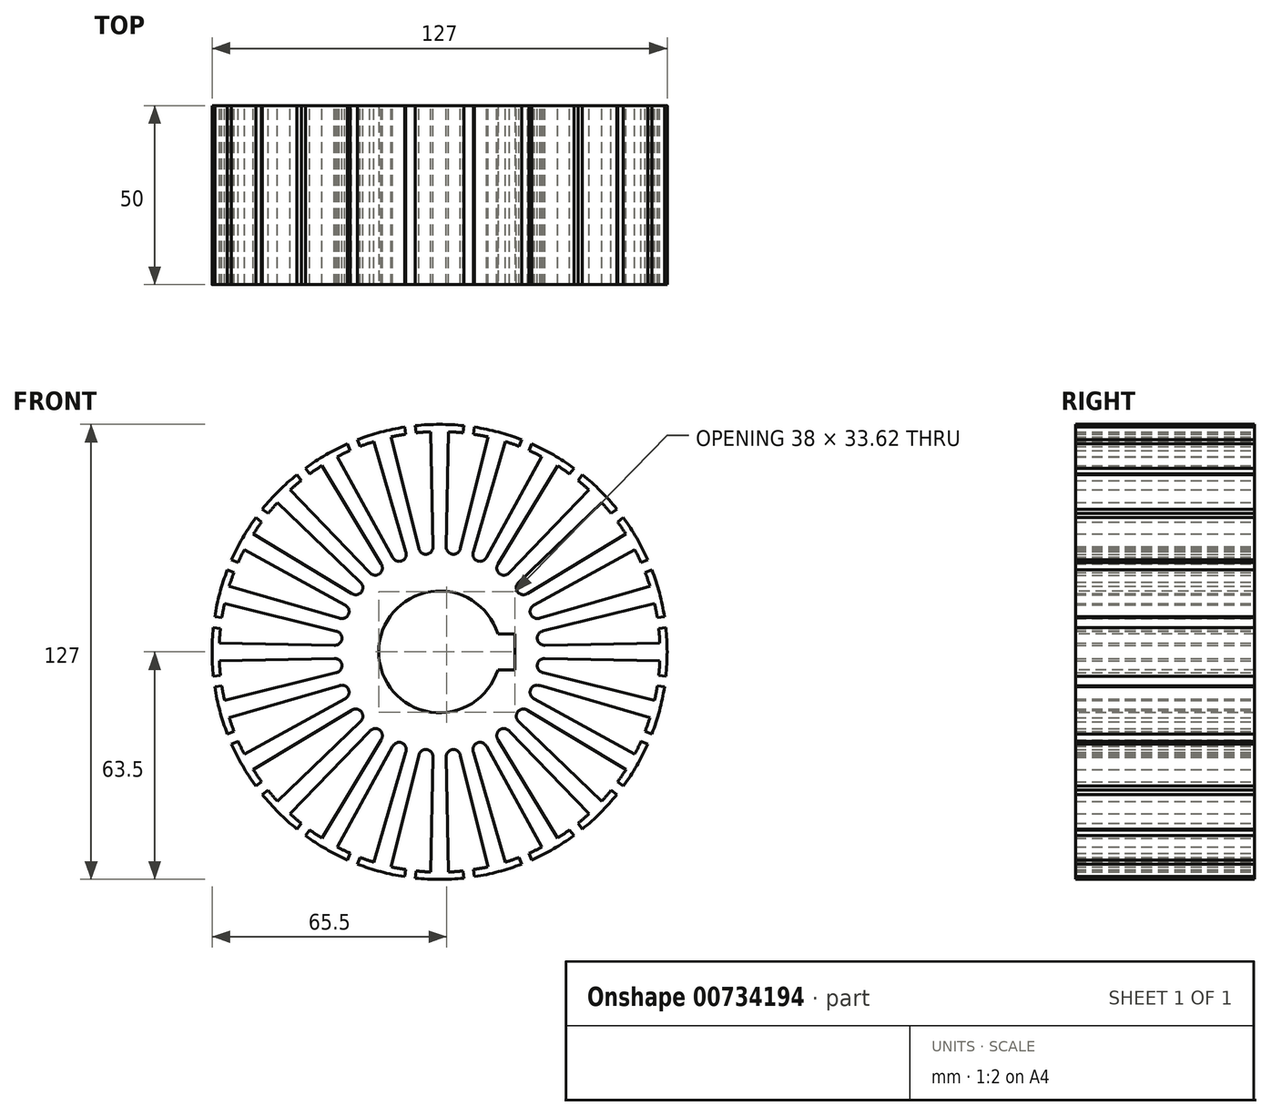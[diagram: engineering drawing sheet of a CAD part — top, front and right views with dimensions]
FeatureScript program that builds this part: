
annotation { "Feature Type Name" : "Feature", "Feature Type Description" : "" }
export const myFeature = defineFeature(function(context is Context, id is Id, definition is map)
    precondition{}
    {
        {
            var Q0;
            Q0=qCreatedBy(makeId("Front.planeOp"),FACE);
            var sketch = newSketch(context, id + "F0", { "sketchPlane" : qUnion([Q0])});
            skCircle(sketch, "E0", {"center": v(0, 0) * mm, "radius": 17 * mm});
            skArc(sketch, "E1", {"start": v(-9.51, 60.76) * mm, "mid": v(-11.5, 60.41) * mm, "end": v(-13.48, 60) * mm});
            skArc(sketch, "E2", {"start": v(1.86, 29.44) * mm, "mid": v(2.28, 28) * mm, "end": v(3.59, 27.26) * mm});
            skArc(sketch, "E3.MirrorC", {"start": v(-1.86, 29.44) * mm, "mid": v(-2.28, 28) * mm, "end": v(-3.59, 27.26) * mm});
            skArc(sketch, "E4.MirrorC", {"start": v(13.1, 26.43) * mm, "mid": v(10.52, 25.4) * mm, "end": v(9.42, 27.96) * mm});
            skArc(sketch, "E5.MirrorC", {"start": v(16.33, 24.57) * mm, "mid": v(16.74, 21.82) * mm, "end": v(19.5, 22.13) * mm});
            skArc(sketch, "E6.MirrorC", {"start": v(24.57, 16.33) * mm, "mid": v(23.1, 15.98) * mm, "end": v(21.82, 16.74) * mm});
            skArc(sketch, "E7.MirrorC", {"start": v(26.43, 13.1) * mm, "mid": v(25.4, 10.52) * mm, "end": v(27.96, 9.42) * mm});
            skArc(sketch, "E8.MirrorC", {"start": v(29.44, 1.86) * mm, "mid": v(27.26, 3.59) * mm, "end": v(28.92, 5.82) * mm});
            skArc(sketch, "E9.MirrorC", {"start": v(29.44, -1.86) * mm, "mid": v(27.26, -3.59) * mm, "end": v(28.92, -5.82) * mm});
            skArc(sketch, "E10.MirrorC", {"start": v(26.43, -13.1) * mm, "mid": v(25.4, -10.52) * mm, "end": v(27.96, -9.42) * mm});
            skArc(sketch, "E11.MirrorC", {"start": v(24.57, -16.33) * mm, "mid": v(21.82, -16.74) * mm, "end": v(22.13, -19.5) * mm});
            skArc(sketch, "E12.MirrorC", {"start": v(16.33, -24.57) * mm, "mid": v(16.74, -21.82) * mm, "end": v(19.5, -22.13) * mm});
            skArc(sketch, "E13.MirrorC", {"start": v(13.1, -26.43) * mm, "mid": v(10.52, -25.4) * mm, "end": v(9.42, -27.96) * mm});
            skArc(sketch, "E14.MirrorC", {"start": v(1.86, -29.44) * mm, "mid": v(3.59, -27.26) * mm, "end": v(5.82, -28.92) * mm});
            skArc(sketch, "E15.MirrorC", {"start": v(-1.86, -29.44) * mm, "mid": v(-3.59, -27.26) * mm, "end": v(-5.82, -28.92) * mm});
            skArc(sketch, "E16.MirrorC", {"start": v(-13.1, -26.43) * mm, "mid": v(-10.52, -25.4) * mm, "end": v(-9.42, -27.96) * mm});
            skArc(sketch, "E17.MirrorC", {"start": v(-16.33, -24.57) * mm, "mid": v(-16.74, -21.82) * mm, "end": v(-19.5, -22.13) * mm});
            skArc(sketch, "E18.MirrorC", {"start": v(-24.57, -16.33) * mm, "mid": v(-21.82, -16.74) * mm, "end": v(-22.13, -19.5) * mm});
            skArc(sketch, "E19.MirrorC", {"start": v(-26.43, -13.1) * mm, "mid": v(-25.4, -10.52) * mm, "end": v(-27.96, -9.42) * mm});
            skArc(sketch, "E20.MirrorC", {"start": v(-29.44, -1.86) * mm, "mid": v(-27.26, -3.59) * mm, "end": v(-28.92, -5.82) * mm});
            skArc(sketch, "E21.MirrorC", {"start": v(-29.44, 1.86) * mm, "mid": v(-27.26, 3.59) * mm, "end": v(-28.92, 5.82) * mm});
            skArc(sketch, "E22.MirrorC", {"start": v(-26.43, 13.1) * mm, "mid": v(-25.4, 10.52) * mm, "end": v(-27.96, 9.42) * mm});
            skArc(sketch, "E23.MirrorC", {"start": v(-24.57, 16.33) * mm, "mid": v(-21.82, 16.74) * mm, "end": v(-22.13, 19.5) * mm});
            skArc(sketch, "E24.MirrorC", {"start": v(-13.1, 26.43) * mm, "mid": v(-10.52, 25.4) * mm, "end": v(-9.42, 27.96) * mm});
            skArc(sketch, "E25.MirrorC", {"start": v(-16.33, 24.57) * mm, "mid": v(-16.74, 21.82) * mm, "end": v(-19.5, 22.13) * mm});
            skLineSegment(sketch, "E26", {"start": v(-2.5, 61.45) * mm, "end": v(-1.86, 29.44) * mm});
            skLineSegment(sketch, "E27", {"start": v(2.5, 61.45) * mm, "end": v(1.85, 29.44) * mm});
            skLineSegment(sketch, "E28.MirrorCS", {"start": v(13.49, 60) * mm, "end": v(5.83, 28.92) * mm});
            skLineSegment(sketch, "E29.MirrorCS", {"start": v(-13.48, 60) * mm, "end": v(-5.82, 28.92) * mm});
            skLineSegment(sketch, "E30.MirrorCS", {"start": v(18.32, 58.7) * mm, "end": v(9.41, 27.96) * mm});
            skLineSegment(sketch, "E31.MirrorCS", {"start": v(28.56, 54.47) * mm, "end": v(13.12, 26.42) * mm});
            skLineSegment(sketch, "E32.MirrorCS", {"start": v(32.9, 51.96) * mm, "end": v(16.33, 24.57) * mm});
            skLineSegment(sketch, "E33.MirrorCS", {"start": v(41.68, 45.22) * mm, "end": v(19.5, 22.13) * mm});
            skLineSegment(sketch, "E34.MirrorCS", {"start": v(45.22, 41.68) * mm, "end": v(22.13, 19.5) * mm});
            skLineSegment(sketch, "E35.MirrorCS", {"start": v(54.47, 28.56) * mm, "end": v(26.42, 13.12) * mm});
            skLineSegment(sketch, "E36.MirrorCS", {"start": v(58.7, 18.32) * mm, "end": v(27.96, 9.41) * mm});
            skLineSegment(sketch, "E37.MirrorCS", {"start": v(60, 13.49) * mm, "end": v(28.92, 5.83) * mm});
            skLineSegment(sketch, "E38.MirrorCS", {"start": v(61.45, 2.5) * mm, "end": v(29.44, 1.85) * mm});
            skLineSegment(sketch, "E39.MirrorCS", {"start": v(61.45, -2.5) * mm, "end": v(29.44, -1.86) * mm});
            skLineSegment(sketch, "E40.MirrorCS", {"start": v(60, -13.48) * mm, "end": v(28.92, -5.82) * mm});
            skLineSegment(sketch, "E41.MirrorCS", {"start": v(58.7, -18.33) * mm, "end": v(27.96, -9.42) * mm});
            skLineSegment(sketch, "E42.MirrorCS", {"start": v(54.47, -28.55) * mm, "end": v(26.43, -13.1) * mm});
            skLineSegment(sketch, "E43.MirrorCS", {"start": v(51.97, -32.89) * mm, "end": v(24.57, -16.33) * mm});
            skLineSegment(sketch, "E44.MirrorCS", {"start": v(45.22, -41.68) * mm, "end": v(22.13, -19.5) * mm});
            skLineSegment(sketch, "E45.MirrorCS", {"start": v(41.68, -45.22) * mm, "end": v(19.5, -22.13) * mm});
            skLineSegment(sketch, "E46.MirrorCS", {"start": v(32.89, -51.97) * mm, "end": v(16.33, -24.57) * mm});
            skLineSegment(sketch, "E47.MirrorCS", {"start": v(51.96, 32.9) * mm, "end": v(24.57, 16.33) * mm});
            skLineSegment(sketch, "E48.MirrorCS", {"start": v(28.56, -54.47) * mm, "end": v(13.12, -26.42) * mm});
            skLineSegment(sketch, "E49.MirrorCS", {"start": v(18.32, -58.7) * mm, "end": v(9.41, -27.96) * mm});
            skLineSegment(sketch, "E50.MirrorCS", {"start": v(13.49, -60) * mm, "end": v(5.83, -28.92) * mm});
            skLineSegment(sketch, "E51.MirrorCS", {"start": v(2.5, -61.45) * mm, "end": v(1.85, -29.44) * mm});
            skLineSegment(sketch, "E52.MirrorCS", {"start": v(-2.5, -61.45) * mm, "end": v(-1.85, -29.44) * mm});
            skLineSegment(sketch, "E53.MirrorCS", {"start": v(-13.49, -60) * mm, "end": v(-5.83, -28.92) * mm});
            skLineSegment(sketch, "E54.MirrorCS", {"start": v(-18.32, -58.7) * mm, "end": v(-9.41, -27.96) * mm});
            skLineSegment(sketch, "E55.MirrorCS", {"start": v(-28.56, -54.47) * mm, "end": v(-13.12, -26.42) * mm});
            skLineSegment(sketch, "E56.MirrorCS", {"start": v(-32.89, -51.97) * mm, "end": v(-16.33, -24.57) * mm});
            skLineSegment(sketch, "E57.MirrorCS", {"start": v(-41.68, -45.22) * mm, "end": v(-19.5, -22.13) * mm});
            skLineSegment(sketch, "E58.MirrorCS", {"start": v(-45.22, -41.68) * mm, "end": v(-22.13, -19.5) * mm});
            skLineSegment(sketch, "E59.MirrorCS", {"start": v(-51.97, -32.89) * mm, "end": v(-24.57, -16.33) * mm});
            skLineSegment(sketch, "E60.MirrorCS", {"start": v(-54.47, -28.56) * mm, "end": v(-26.42, -13.12) * mm});
            skLineSegment(sketch, "E61.MirrorCS", {"start": v(-58.7, -18.32) * mm, "end": v(-27.96, -9.41) * mm});
            skLineSegment(sketch, "E62.MirrorCS", {"start": v(-60, -13.49) * mm, "end": v(-28.92, -5.83) * mm});
            skLineSegment(sketch, "E63.MirrorCS", {"start": v(-61.45, -2.5) * mm, "end": v(-29.44, -1.85) * mm});
            skLineSegment(sketch, "E64.MirrorCS", {"start": v(-61.45, 2.5) * mm, "end": v(-29.44, 1.85) * mm});
            skLineSegment(sketch, "E65.MirrorCS", {"start": v(-60, 13.49) * mm, "end": v(-28.92, 5.83) * mm});
            skLineSegment(sketch, "E66.MirrorCS", {"start": v(-58.7, 18.32) * mm, "end": v(-27.96, 9.41) * mm});
            skLineSegment(sketch, "E67.MirrorCS", {"start": v(-54.47, 28.56) * mm, "end": v(-26.42, 13.12) * mm});
            skLineSegment(sketch, "E68.MirrorCS", {"start": v(-51.97, 32.89) * mm, "end": v(-24.57, 16.33) * mm});
            skLineSegment(sketch, "E69.MirrorCS", {"start": v(-45.22, 41.68) * mm, "end": v(-22.13, 19.5) * mm});
            skLineSegment(sketch, "E70.MirrorCS", {"start": v(-41.68, 45.22) * mm, "end": v(-19.5, 22.13) * mm});
            skLineSegment(sketch, "E71.MirrorCS", {"start": v(-32.89, 51.97) * mm, "end": v(-16.33, 24.57) * mm});
            skLineSegment(sketch, "E72.MirrorCS", {"start": v(-28.56, 54.47) * mm, "end": v(-13.12, 26.42) * mm});
            skLineSegment(sketch, "E73.MirrorCS", {"start": v(-18.32, 58.7) * mm, "end": v(-9.41, 27.96) * mm});
            skArc(sketch, "E74.MirrorCS", {"start": v(22.13, 19.5) * mm, "mid": v(21.42, 18.19) * mm, "end": v(21.82, 16.74) * mm});
            skLineSegment(sketch, "E75.MirrorCS", {"start": v(-6.8, 63.13) * mm, "end": v(-6.54, 61.15) * mm});
            skLineSegment(sketch, "E76.MirrorCS", {"start": v(-9.77, 62.74) * mm, "end": v(-9.51, 60.76) * mm});
            skLineSegment(sketch, "E77.MirrorCS", {"start": v(-22.9, 59.22) * mm, "end": v(-22.14, 57.38) * mm});
            skLineSegment(sketch, "E78.MirrorCS", {"start": v(-25.69, 58.1) * mm, "end": v(-24.91, 56.23) * mm});
            skLineSegment(sketch, "E79.MirrorCS", {"start": v(-37.47, 51.3) * mm, "end": v(-36.24, 49.69) * mm});
            skLineSegment(sketch, "E80.MirrorCS", {"start": v(-39.84, 49.45) * mm, "end": v(-38.62, 47.86) * mm});
            skLineSegment(sketch, "E81.MirrorCS", {"start": v(-49.45, 39.84) * mm, "end": v(-47.86, 38.62) * mm});
            skLineSegment(sketch, "E82.MirrorCS", {"start": v(-51.3, 37.47) * mm, "end": v(-49.69, 36.24) * mm});
            skLineSegment(sketch, "E83.MirrorCS", {"start": v(-59.22, 22.9) * mm, "end": v(-57.38, 22.14) * mm});
            skLineSegment(sketch, "E84.MirrorCS", {"start": v(-58.1, 25.69) * mm, "end": v(-56.23, 24.91) * mm});
            skLineSegment(sketch, "E85.MirrorCS", {"start": v(-62.74, 9.77) * mm, "end": v(-60.76, 9.51) * mm});
            skLineSegment(sketch, "E86.MirrorCS", {"start": v(-63.15, 6.8) * mm, "end": v(-61.15, 6.54) * mm});
            skLineSegment(sketch, "E87.MirrorCS", {"start": v(-63.15, -6.8) * mm, "end": v(-61.15, -6.54) * mm});
            skLineSegment(sketch, "E88.MirrorCS", {"start": v(-62.74, -9.77) * mm, "end": v(-60.76, -9.51) * mm});
            skLineSegment(sketch, "E89.MirrorCS", {"start": v(-59.22, -22.9) * mm, "end": v(-57.38, -22.14) * mm});
            skLineSegment(sketch, "E90.MirrorCS", {"start": v(-58.1, -25.69) * mm, "end": v(-56.23, -24.91) * mm});
            skLineSegment(sketch, "E91.MirrorCS", {"start": v(-51.3, -37.47) * mm, "end": v(-49.69, -36.24) * mm});
            skLineSegment(sketch, "E92.MirrorCS", {"start": v(-49.45, -39.84) * mm, "end": v(-47.86, -38.62) * mm});
            skLineSegment(sketch, "E93.MirrorCS", {"start": v(-39.84, -49.45) * mm, "end": v(-38.62, -47.86) * mm});
            skLineSegment(sketch, "E94.MirrorCS", {"start": v(-37.47, -51.3) * mm, "end": v(-36.24, -49.69) * mm});
            skLineSegment(sketch, "E95.MirrorCS", {"start": v(-25.69, -58.1) * mm, "end": v(-24.91, -56.23) * mm});
            skLineSegment(sketch, "E96.MirrorCS", {"start": v(-22.9, -59.22) * mm, "end": v(-22.14, -57.38) * mm});
            skLineSegment(sketch, "E97.MirrorCS", {"start": v(-9.77, -62.74) * mm, "end": v(-9.51, -60.76) * mm});
            skLineSegment(sketch, "E98.MirrorCS", {"start": v(-6.8, -63.15) * mm, "end": v(-6.54, -61.15) * mm});
            skLineSegment(sketch, "E99.MirrorCS", {"start": v(6.8, -63.15) * mm, "end": v(6.54, -61.15) * mm});
            skLineSegment(sketch, "E100.MirrorCS", {"start": v(9.77, -62.74) * mm, "end": v(9.51, -60.76) * mm});
            skLineSegment(sketch, "E101.MirrorCS", {"start": v(22.9, -59.22) * mm, "end": v(22.14, -57.38) * mm});
            skLineSegment(sketch, "E102.MirrorCS", {"start": v(25.69, -58.1) * mm, "end": v(24.91, -56.23) * mm});
            skLineSegment(sketch, "E103.MirrorCS", {"start": v(37.47, -51.3) * mm, "end": v(36.24, -49.69) * mm});
            skLineSegment(sketch, "E104.MirrorCS", {"start": v(39.84, -49.45) * mm, "end": v(38.62, -47.86) * mm});
            skLineSegment(sketch, "E105.MirrorCS", {"start": v(49.45, -39.84) * mm, "end": v(47.86, -38.62) * mm});
            skLineSegment(sketch, "E106.MirrorCS", {"start": v(51.3, -37.47) * mm, "end": v(49.69, -36.24) * mm});
            skLineSegment(sketch, "E107.MirrorCS", {"start": v(58.1, -25.69) * mm, "end": v(56.23, -24.91) * mm});
            skLineSegment(sketch, "E108.MirrorCS", {"start": v(59.22, -22.9) * mm, "end": v(57.38, -22.14) * mm});
            skLineSegment(sketch, "E109.MirrorCS", {"start": v(63.15, -6.8) * mm, "end": v(61.15, -6.54) * mm});
            skLineSegment(sketch, "E110.MirrorCS", {"start": v(62.74, -9.77) * mm, "end": v(60.76, -9.51) * mm});
            skLineSegment(sketch, "E111.MirrorCS", {"start": v(63.15, 6.8) * mm, "end": v(61.15, 6.54) * mm});
            skLineSegment(sketch, "E112.MirrorCS", {"start": v(62.74, 9.77) * mm, "end": v(60.76, 9.51) * mm});
            skLineSegment(sketch, "E113.MirrorCS", {"start": v(59.22, 22.9) * mm, "end": v(57.38, 22.14) * mm});
            skLineSegment(sketch, "E114.MirrorCS", {"start": v(58.1, 25.69) * mm, "end": v(56.23, 24.91) * mm});
            skLineSegment(sketch, "E115.MirrorCS", {"start": v(51.3, 37.47) * mm, "end": v(49.69, 36.24) * mm});
            skLineSegment(sketch, "E116.MirrorCS", {"start": v(49.45, 39.84) * mm, "end": v(47.86, 38.62) * mm});
            skLineSegment(sketch, "E117.MirrorCS", {"start": v(39.84, 49.45) * mm, "end": v(38.62, 47.86) * mm});
            skLineSegment(sketch, "E118.MirrorCS", {"start": v(37.47, 51.3) * mm, "end": v(36.24, 49.69) * mm});
            skLineSegment(sketch, "E119.MirrorCS", {"start": v(6.8, 63.13) * mm, "end": v(6.54, 61.15) * mm});
            skLineSegment(sketch, "E120.MirrorCS", {"start": v(9.77, 62.74) * mm, "end": v(9.51, 60.76) * mm});
            skLineSegment(sketch, "E121.MirrorCS", {"start": v(22.9, 59.22) * mm, "end": v(22.14, 57.38) * mm});
            skLineSegment(sketch, "E122.MirrorCS", {"start": v(25.69, 58.1) * mm, "end": v(24.91, 56.23) * mm});
            skArc(sketch, "E123.trimOffspring", {"start": v(-24.91, 56.23) * mm, "mid": v(-26.75, 55.38) * mm, "end": v(-28.56, 54.47) * mm});
            skArc(sketch, "E124.trimOffspring", {"start": v(-25.68, 58.08) * mm, "mid": v(-31.75, 55) * mm, "end": v(-37.46, 51.28) * mm});
            skArc(sketch, "E125.trimOffspring", {"start": v(-38.62, 47.86) * mm, "mid": v(-40.17, 46.57) * mm, "end": v(-41.68, 45.22) * mm});
            skArc(sketch, "E126.trimOffspring", {"start": v(-39.84, 49.45) * mm, "mid": v(-44.9, 44.9) * mm, "end": v(-49.45, 39.84) * mm});
            skArc(sketch, "E127.trimOffspring", {"start": v(-57.38, 22.14) * mm, "mid": v(-58.07, 20.24) * mm, "end": v(-58.7, 18.32) * mm});
            skArc(sketch, "E128.trimOffspring", {"start": v(-59.22, 22.9) * mm, "mid": v(-61.34, 16.44) * mm, "end": v(-62.74, 9.77) * mm});
            skArc(sketch, "E129.trimOffspring", {"start": v(-51.28, 37.46) * mm, "mid": v(-55, 31.75) * mm, "end": v(-58.08, 25.68) * mm});
            skArc(sketch, "E130.trimOffspring", {"start": v(-49.69, 36.24) * mm, "mid": v(-50.86, 34.58) * mm, "end": v(-51.97, 32.89) * mm});
            skArc(sketch, "E131.trimOffspring", {"start": v(-61.15, 6.54) * mm, "mid": v(-61.33, 4.52) * mm, "end": v(-61.45, 2.5) * mm});
            skArc(sketch, "E132.trimOffspring", {"start": v(-63.13, 6.8) * mm, "mid": v(-63.5, 0) * mm, "end": v(-63.13, -6.8) * mm});
            skArc(sketch, "E133.trimOffspring", {"start": v(-60.76, -9.51) * mm, "mid": v(-60.41, -11.5) * mm, "end": v(-60, -13.49) * mm});
            skArc(sketch, "E134.trimOffspring", {"start": v(-56.23, -24.91) * mm, "mid": v(-55.38, -26.75) * mm, "end": v(-54.47, -28.56) * mm});
            skArc(sketch, "E135.trimOffspring", {"start": v(-62.74, -9.77) * mm, "mid": v(-61.34, -16.44) * mm, "end": v(-59.22, -22.9) * mm});
            skArc(sketch, "E136.trimOffspring", {"start": v(-58.08, -25.68) * mm, "mid": v(-55, -31.75) * mm, "end": v(-51.28, -37.46) * mm});
            skArc(sketch, "E137.trimOffspring", {"start": v(-49.45, -39.84) * mm, "mid": v(-44.9, -44.9) * mm, "end": v(-39.84, -49.45) * mm});
            skArc(sketch, "E138.trimOffspring", {"start": v(-47.86, -38.62) * mm, "mid": v(-46.57, -40.17) * mm, "end": v(-45.22, -41.68) * mm});
            skArc(sketch, "E139.trimOffspring", {"start": v(-37.46, -51.28) * mm, "mid": v(-31.75, -55) * mm, "end": v(-25.68, -58.08) * mm});
            skArc(sketch, "E140.trimOffspring", {"start": v(-36.24, -49.69) * mm, "mid": v(-34.58, -50.86) * mm, "end": v(-32.89, -51.97) * mm});
            skArc(sketch, "E141.trimOffspring", {"start": v(-22.14, -57.38) * mm, "mid": v(-20.24, -58.07) * mm, "end": v(-18.32, -58.7) * mm});
            skArc(sketch, "E142.trimOffspring", {"start": v(-22.9, -59.22) * mm, "mid": v(-16.44, -61.34) * mm, "end": v(-9.77, -62.74) * mm});
            skArc(sketch, "E143.trimOffspring", {"start": v(-6.54, -61.15) * mm, "mid": v(-4.52, -61.33) * mm, "end": v(-2.5, -61.45) * mm});
            skArc(sketch, "E144.trimOffspring", {"start": v(-6.8, -63.13) * mm, "mid": v(0, -63.5) * mm, "end": v(6.8, -63.13) * mm});
            skArc(sketch, "E145.trimOffspring", {"start": v(9.51, -60.76) * mm, "mid": v(11.5, -60.41) * mm, "end": v(13.49, -60) * mm});
            skArc(sketch, "E146.trimOffspring", {"start": v(9.77, -62.74) * mm, "mid": v(16.44, -61.34) * mm, "end": v(22.9, -59.22) * mm});
            skArc(sketch, "E147.trimOffspring", {"start": v(24.91, -56.23) * mm, "mid": v(26.75, -55.38) * mm, "end": v(28.56, -54.47) * mm});
            skArc(sketch, "E148.trimOffspring", {"start": v(25.68, -58.08) * mm, "mid": v(31.75, -55) * mm, "end": v(37.46, -51.28) * mm});
            skArc(sketch, "E149.trimOffspring", {"start": v(38.62, -47.86) * mm, "mid": v(40.17, -46.57) * mm, "end": v(41.68, -45.22) * mm});
            skArc(sketch, "E150.trimOffspring", {"start": v(39.84, -49.45) * mm, "mid": v(44.9, -44.9) * mm, "end": v(49.45, -39.84) * mm});
            skArc(sketch, "E151.trimOffspring", {"start": v(49.69, -36.24) * mm, "mid": v(50.86, -34.58) * mm, "end": v(51.97, -32.89) * mm});
            skArc(sketch, "E152.trimOffspring", {"start": v(51.28, -37.46) * mm, "mid": v(55, -31.75) * mm, "end": v(58.08, -25.68) * mm});
            skArc(sketch, "E153.trimOffspring", {"start": v(57.38, -22.14) * mm, "mid": v(58.07, -20.24) * mm, "end": v(58.7, -18.33) * mm});
            skArc(sketch, "E154.trimOffspring", {"start": v(59.22, -22.9) * mm, "mid": v(61.34, -16.44) * mm, "end": v(62.74, -9.77) * mm});
            skArc(sketch, "E155.trimOffspring", {"start": v(61.15, -6.54) * mm, "mid": v(61.33, -4.52) * mm, "end": v(61.45, -2.5) * mm});
            skArc(sketch, "E156.trimOffspring", {"start": v(63.13, -6.8) * mm, "mid": v(63.5, 0) * mm, "end": v(63.13, 6.8) * mm});
            skArc(sketch, "E157.trimOffspring", {"start": v(60.76, 9.51) * mm, "mid": v(60.41, 11.5) * mm, "end": v(60, 13.49) * mm});
            skArc(sketch, "E158.trimOffspring", {"start": v(56.23, 24.91) * mm, "mid": v(55.38, 26.75) * mm, "end": v(54.47, 28.56) * mm});
            skArc(sketch, "E159.trimOffspring", {"start": v(58.08, 25.68) * mm, "mid": v(55, 31.75) * mm, "end": v(51.28, 37.46) * mm});
            skArc(sketch, "E160.trimOffspring", {"start": v(47.86, 38.62) * mm, "mid": v(46.57, 40.17) * mm, "end": v(45.22, 41.68) * mm});
            skArc(sketch, "E161.trimOffspring", {"start": v(49.45, 39.84) * mm, "mid": v(44.9, 44.9) * mm, "end": v(39.84, 49.45) * mm});
            skArc(sketch, "E162.trimOffspring", {"start": v(36.24, 49.69) * mm, "mid": v(34.59, 50.85) * mm, "end": v(32.9, 51.96) * mm});
            skArc(sketch, "E163.trimOffspring", {"start": v(37.46, 51.28) * mm, "mid": v(31.75, 55) * mm, "end": v(25.68, 58.08) * mm});
            skArc(sketch, "E164.trimOffspring", {"start": v(22.14, 57.38) * mm, "mid": v(20.24, 58.07) * mm, "end": v(18.32, 58.7) * mm});
            skArc(sketch, "E165.trimOffspring", {"start": v(22.9, 59.22) * mm, "mid": v(16.44, 61.34) * mm, "end": v(9.77, 62.74) * mm});
            skArc(sketch, "E166.trimOffspring", {"start": v(6.8, 63.13) * mm, "mid": v(0, 63.5) * mm, "end": v(-6.8, 63.13) * mm});
            skArc(sketch, "E167.trimOffspring", {"start": v(6.54, 61.15) * mm, "mid": v(4.52, 61.33) * mm, "end": v(2.5, 61.45) * mm});
            skArc(sketch, "E168", {"start": v(-22.9, 59.22) * mm, "mid": v(-16.44, 61.34) * mm, "end": v(-9.77, 62.74) * mm});
            skArc(sketch, "E169.trimOffspring", {"start": v(-45.22, 41.68) * mm, "mid": v(-46.57, 40.17) * mm, "end": v(-47.86, 38.62) * mm});
            skArc(sketch, "E170.trimOffspring", {"start": v(-32.89, 51.97) * mm, "mid": v(-34.58, 50.86) * mm, "end": v(-36.24, 49.69) * mm});
            skArc(sketch, "E171.trimOffspring", {"start": v(-54.47, 28.56) * mm, "mid": v(-55.38, 26.75) * mm, "end": v(-56.23, 24.91) * mm});
            skArc(sketch, "E172.trimOffspring", {"start": v(-60, 13.49) * mm, "mid": v(-60.41, 11.5) * mm, "end": v(-60.76, 9.51) * mm});
            skArc(sketch, "E173.trimOffspring", {"start": v(-58.7, -18.32) * mm, "mid": v(-58.07, -20.24) * mm, "end": v(-57.38, -22.14) * mm});
            skArc(sketch, "E174.trimOffspring", {"start": v(-51.97, -32.89) * mm, "mid": v(-50.86, -34.58) * mm, "end": v(-49.69, -36.24) * mm});
            skArc(sketch, "E175.trimOffspring", {"start": v(-61.45, -2.5) * mm, "mid": v(-61.33, -4.52) * mm, "end": v(-61.15, -6.54) * mm});
            skArc(sketch, "E176.trimOffspring", {"start": v(-41.68, -45.22) * mm, "mid": v(-40.17, -46.57) * mm, "end": v(-38.62, -47.86) * mm});
            skArc(sketch, "E177.trimOffspring", {"start": v(-28.56, -54.47) * mm, "mid": v(-26.75, -55.38) * mm, "end": v(-24.91, -56.23) * mm});
            skArc(sketch, "E178.trimOffspring", {"start": v(-13.49, -60) * mm, "mid": v(-11.5, -60.41) * mm, "end": v(-9.51, -60.76) * mm});
            skArc(sketch, "E179.trimOffspring", {"start": v(2.5, -61.45) * mm, "mid": v(4.52, -61.33) * mm, "end": v(6.54, -61.15) * mm});
            skArc(sketch, "E180.trimOffspring", {"start": v(18.32, -58.7) * mm, "mid": v(20.24, -58.07) * mm, "end": v(22.14, -57.38) * mm});
            skArc(sketch, "E181.trimOffspring", {"start": v(32.89, -51.97) * mm, "mid": v(34.58, -50.86) * mm, "end": v(36.24, -49.69) * mm});
            skArc(sketch, "E182.trimOffspring", {"start": v(45.22, -41.68) * mm, "mid": v(46.57, -40.17) * mm, "end": v(47.86, -38.62) * mm});
            skArc(sketch, "E183.trimOffspring", {"start": v(54.47, -28.55) * mm, "mid": v(55.38, -26.75) * mm, "end": v(56.23, -24.91) * mm});
            skArc(sketch, "E184.trimOffspring", {"start": v(60, -13.48) * mm, "mid": v(60.41, -11.5) * mm, "end": v(60.76, -9.51) * mm});
            skArc(sketch, "E185.trimOffspring", {"start": v(61.45, 2.5) * mm, "mid": v(61.33, 4.52) * mm, "end": v(61.15, 6.54) * mm});
            skArc(sketch, "E186.trimOffspring", {"start": v(58.7, 18.32) * mm, "mid": v(58.07, 20.24) * mm, "end": v(57.38, 22.14) * mm});
            skArc(sketch, "E187.trimOffspring", {"start": v(51.96, 32.9) * mm, "mid": v(50.85, 34.59) * mm, "end": v(49.69, 36.24) * mm});
            skArc(sketch, "E188.trimOffspring", {"start": v(41.68, 45.22) * mm, "mid": v(40.17, 46.57) * mm, "end": v(38.62, 47.86) * mm});
            skArc(sketch, "E189.trimOffspring", {"start": v(28.56, 54.47) * mm, "mid": v(26.75, 55.38) * mm, "end": v(24.91, 56.23) * mm});
            skArc(sketch, "E190.trimOffspring", {"start": v(13.49, 60) * mm, "mid": v(11.5, 60.41) * mm, "end": v(9.51, 60.76) * mm});
            skArc(sketch, "E191.trimOffspring", {"start": v(-2.5, 61.45) * mm, "mid": v(-4.52, 61.33) * mm, "end": v(-6.54, 61.15) * mm});
            skArc(sketch, "E192.trimOffspring", {"start": v(-18.32, 58.7) * mm, "mid": v(-20.24, 58.07) * mm, "end": v(-22.14, 57.38) * mm});
            skArc(sketch, "E193", {"start": v(59.22, 22.9) * mm, "mid": v(61.34, 16.44) * mm, "end": v(62.74, 9.77) * mm});
            skLineSegment(sketch, "E194", {"start": v(3.59, 27.26) * mm, "end": v(0, 0) * mm});
            skLineSegment(sketch, "E195", {"start": v(-3.59, 27.26) * mm, "end": v(0, 0) * mm});
            skLineSegment(sketch, "E196", {"start": v(1.85, 29.44) * mm, "end": v(1.86, 29.44) * mm});
            skSolve(sketch);
        }
        {
            var Q0;
            Q0=qSketchRegion(id+"F0",true);
            extrude(context, id + "F1", {"entities" : qUnion([Q0]), "depth" : 50 * mm, "offsetDistance" : 25 * mm});
        }
        {
            var Q0;
            Q0=makeQuery(id+"F1.opExtrude","SWEPT_BODY",BODY,{"disambiguationData":[OSD([sQuery(id+"F0.wireOp",EDGE,"E0"),sQuery(id+"F0.wireOp",EDGE,"E2"),sQuery(id+"F0.wireOp",EDGE,"E3.MirrorC"),sQuery(id+"F0.wireOp",EDGE,"E26"),sQuery(id+"F0.wireOp",EDGE,"E27"),sQuery(id+"F0.wireOp",EDGE,"E75.MirrorCS"),sQuery(id+"F0.wireOp",EDGE,"E119.MirrorCS"),sQuery(id+"F0.wireOp",EDGE,"E166.trimOffspring"),sQuery(id+"F0.wireOp",EDGE,"E167.trimOffspring"),sQuery(id+"F0.wireOp",EDGE,"E191.trimOffspring"),sQuery(id+"F0.wireOp",EDGE,"E194"),sQuery(id+"F0.wireOp",EDGE,"E195"),sQuery(id+"F0.wireOp",EDGE,"E196")])]});
            var Q1;
            Q1=makeQuery(id+"F1.opExtrude","SWEPT_FACE",FACE,{"disambiguationData":[OSD([sQuery(id+"F0.wireOp",EDGE,"E0")])]});
            circularPattern(context, id + "F2", {"entities" : qUnion([Q0]), "axis" : qUnion([Q1]), "angle" : 360 * degree, "instanceCount" : 24, "equalSpace" : true});
        }
        {
            var Q0;
            Q0=makeQuery(id+"F1.opExtrude","SWEPT_BODY",BODY,{"disambiguationData":[OSD([sQuery(id+"F0.wireOp",EDGE,"E0"),sQuery(id+"F0.wireOp",EDGE,"E2"),sQuery(id+"F0.wireOp",EDGE,"E3.MirrorC"),sQuery(id+"F0.wireOp",EDGE,"E26"),sQuery(id+"F0.wireOp",EDGE,"E27"),sQuery(id+"F0.wireOp",EDGE,"E75.MirrorCS"),sQuery(id+"F0.wireOp",EDGE,"E119.MirrorCS"),sQuery(id+"F0.wireOp",EDGE,"E166.trimOffspring"),sQuery(id+"F0.wireOp",EDGE,"E167.trimOffspring"),sQuery(id+"F0.wireOp",EDGE,"E191.trimOffspring"),sQuery(id+"F0.wireOp",EDGE,"E194"),sQuery(id+"F0.wireOp",EDGE,"E195"),sQuery(id+"F0.wireOp",EDGE,"E196")])]});
            var Q1;
            Q1=makeQuery(id+"F2.opPattern","COPY",BODY,{"derivedFrom":makeQuery(id+"F1.opExtrude","SWEPT_BODY",BODY,{"disambiguationData":[OSD([sQuery(id+"F0.wireOp",EDGE,"E0"),sQuery(id+"F0.wireOp",EDGE,"E2"),sQuery(id+"F0.wireOp",EDGE,"E3.MirrorC"),sQuery(id+"F0.wireOp",EDGE,"E26"),sQuery(id+"F0.wireOp",EDGE,"E27"),sQuery(id+"F0.wireOp",EDGE,"E75.MirrorCS"),sQuery(id+"F0.wireOp",EDGE,"E119.MirrorCS"),sQuery(id+"F0.wireOp",EDGE,"E166.trimOffspring"),sQuery(id+"F0.wireOp",EDGE,"E167.trimOffspring"),sQuery(id+"F0.wireOp",EDGE,"E191.trimOffspring"),sQuery(id+"F0.wireOp",EDGE,"E194"),sQuery(id+"F0.wireOp",EDGE,"E195"),sQuery(id+"F0.wireOp",EDGE,"E196")])]}),"instanceName":"1"});
            var Q2;
            Q2=makeQuery(id+"F2.opPattern","COPY",BODY,{"derivedFrom":makeQuery(id+"F1.opExtrude","SWEPT_BODY",BODY,{"disambiguationData":[OSD([sQuery(id+"F0.wireOp",EDGE,"E0"),sQuery(id+"F0.wireOp",EDGE,"E2"),sQuery(id+"F0.wireOp",EDGE,"E3.MirrorC"),sQuery(id+"F0.wireOp",EDGE,"E26"),sQuery(id+"F0.wireOp",EDGE,"E27"),sQuery(id+"F0.wireOp",EDGE,"E75.MirrorCS"),sQuery(id+"F0.wireOp",EDGE,"E119.MirrorCS"),sQuery(id+"F0.wireOp",EDGE,"E166.trimOffspring"),sQuery(id+"F0.wireOp",EDGE,"E167.trimOffspring"),sQuery(id+"F0.wireOp",EDGE,"E191.trimOffspring"),sQuery(id+"F0.wireOp",EDGE,"E194"),sQuery(id+"F0.wireOp",EDGE,"E195"),sQuery(id+"F0.wireOp",EDGE,"E196")])]}),"instanceName":"2"});
            var Q3;
            Q3=makeQuery(id+"F2.opPattern","COPY",BODY,{"derivedFrom":makeQuery(id+"F1.opExtrude","SWEPT_BODY",BODY,{"disambiguationData":[OSD([sQuery(id+"F0.wireOp",EDGE,"E0"),sQuery(id+"F0.wireOp",EDGE,"E2"),sQuery(id+"F0.wireOp",EDGE,"E3.MirrorC"),sQuery(id+"F0.wireOp",EDGE,"E26"),sQuery(id+"F0.wireOp",EDGE,"E27"),sQuery(id+"F0.wireOp",EDGE,"E75.MirrorCS"),sQuery(id+"F0.wireOp",EDGE,"E119.MirrorCS"),sQuery(id+"F0.wireOp",EDGE,"E166.trimOffspring"),sQuery(id+"F0.wireOp",EDGE,"E167.trimOffspring"),sQuery(id+"F0.wireOp",EDGE,"E191.trimOffspring"),sQuery(id+"F0.wireOp",EDGE,"E194"),sQuery(id+"F0.wireOp",EDGE,"E195"),sQuery(id+"F0.wireOp",EDGE,"E196")])]}),"instanceName":"3"});
            var Q4;
            Q4=makeQuery(id+"F2.opPattern","COPY",BODY,{"derivedFrom":makeQuery(id+"F1.opExtrude","SWEPT_BODY",BODY,{"disambiguationData":[OSD([sQuery(id+"F0.wireOp",EDGE,"E0"),sQuery(id+"F0.wireOp",EDGE,"E2"),sQuery(id+"F0.wireOp",EDGE,"E3.MirrorC"),sQuery(id+"F0.wireOp",EDGE,"E26"),sQuery(id+"F0.wireOp",EDGE,"E27"),sQuery(id+"F0.wireOp",EDGE,"E75.MirrorCS"),sQuery(id+"F0.wireOp",EDGE,"E119.MirrorCS"),sQuery(id+"F0.wireOp",EDGE,"E166.trimOffspring"),sQuery(id+"F0.wireOp",EDGE,"E167.trimOffspring"),sQuery(id+"F0.wireOp",EDGE,"E191.trimOffspring"),sQuery(id+"F0.wireOp",EDGE,"E194"),sQuery(id+"F0.wireOp",EDGE,"E195"),sQuery(id+"F0.wireOp",EDGE,"E196")])]}),"instanceName":"4"});
            var Q5;
            Q5=makeQuery(id+"F2.opPattern","COPY",BODY,{"derivedFrom":makeQuery(id+"F1.opExtrude","SWEPT_BODY",BODY,{"disambiguationData":[OSD([sQuery(id+"F0.wireOp",EDGE,"E0"),sQuery(id+"F0.wireOp",EDGE,"E2"),sQuery(id+"F0.wireOp",EDGE,"E3.MirrorC"),sQuery(id+"F0.wireOp",EDGE,"E26"),sQuery(id+"F0.wireOp",EDGE,"E27"),sQuery(id+"F0.wireOp",EDGE,"E75.MirrorCS"),sQuery(id+"F0.wireOp",EDGE,"E119.MirrorCS"),sQuery(id+"F0.wireOp",EDGE,"E166.trimOffspring"),sQuery(id+"F0.wireOp",EDGE,"E167.trimOffspring"),sQuery(id+"F0.wireOp",EDGE,"E191.trimOffspring"),sQuery(id+"F0.wireOp",EDGE,"E194"),sQuery(id+"F0.wireOp",EDGE,"E195"),sQuery(id+"F0.wireOp",EDGE,"E196")])]}),"instanceName":"6"});
            var Q6;
            Q6=makeQuery(id+"F2.opPattern","COPY",BODY,{"derivedFrom":makeQuery(id+"F1.opExtrude","SWEPT_BODY",BODY,{"disambiguationData":[OSD([sQuery(id+"F0.wireOp",EDGE,"E0"),sQuery(id+"F0.wireOp",EDGE,"E2"),sQuery(id+"F0.wireOp",EDGE,"E3.MirrorC"),sQuery(id+"F0.wireOp",EDGE,"E26"),sQuery(id+"F0.wireOp",EDGE,"E27"),sQuery(id+"F0.wireOp",EDGE,"E75.MirrorCS"),sQuery(id+"F0.wireOp",EDGE,"E119.MirrorCS"),sQuery(id+"F0.wireOp",EDGE,"E166.trimOffspring"),sQuery(id+"F0.wireOp",EDGE,"E167.trimOffspring"),sQuery(id+"F0.wireOp",EDGE,"E191.trimOffspring"),sQuery(id+"F0.wireOp",EDGE,"E194"),sQuery(id+"F0.wireOp",EDGE,"E195"),sQuery(id+"F0.wireOp",EDGE,"E196")])]}),"instanceName":"8"});
            var Q7;
            Q7=makeQuery(id+"F2.opPattern","COPY",BODY,{"derivedFrom":makeQuery(id+"F1.opExtrude","SWEPT_BODY",BODY,{"disambiguationData":[OSD([sQuery(id+"F0.wireOp",EDGE,"E0"),sQuery(id+"F0.wireOp",EDGE,"E2"),sQuery(id+"F0.wireOp",EDGE,"E3.MirrorC"),sQuery(id+"F0.wireOp",EDGE,"E26"),sQuery(id+"F0.wireOp",EDGE,"E27"),sQuery(id+"F0.wireOp",EDGE,"E75.MirrorCS"),sQuery(id+"F0.wireOp",EDGE,"E119.MirrorCS"),sQuery(id+"F0.wireOp",EDGE,"E166.trimOffspring"),sQuery(id+"F0.wireOp",EDGE,"E167.trimOffspring"),sQuery(id+"F0.wireOp",EDGE,"E191.trimOffspring"),sQuery(id+"F0.wireOp",EDGE,"E194"),sQuery(id+"F0.wireOp",EDGE,"E195"),sQuery(id+"F0.wireOp",EDGE,"E196")])]}),"instanceName":"9"});
            var Q8;
            Q8=makeQuery(id+"F2.opPattern","COPY",BODY,{"derivedFrom":makeQuery(id+"F1.opExtrude","SWEPT_BODY",BODY,{"disambiguationData":[OSD([sQuery(id+"F0.wireOp",EDGE,"E0"),sQuery(id+"F0.wireOp",EDGE,"E2"),sQuery(id+"F0.wireOp",EDGE,"E3.MirrorC"),sQuery(id+"F0.wireOp",EDGE,"E26"),sQuery(id+"F0.wireOp",EDGE,"E27"),sQuery(id+"F0.wireOp",EDGE,"E75.MirrorCS"),sQuery(id+"F0.wireOp",EDGE,"E119.MirrorCS"),sQuery(id+"F0.wireOp",EDGE,"E166.trimOffspring"),sQuery(id+"F0.wireOp",EDGE,"E167.trimOffspring"),sQuery(id+"F0.wireOp",EDGE,"E191.trimOffspring"),sQuery(id+"F0.wireOp",EDGE,"E194"),sQuery(id+"F0.wireOp",EDGE,"E195"),sQuery(id+"F0.wireOp",EDGE,"E196")])]}),"instanceName":"11"});
            var Q9;
            Q9=makeQuery(id+"F2.opPattern","COPY",BODY,{"derivedFrom":makeQuery(id+"F1.opExtrude","SWEPT_BODY",BODY,{"disambiguationData":[OSD([sQuery(id+"F0.wireOp",EDGE,"E0"),sQuery(id+"F0.wireOp",EDGE,"E2"),sQuery(id+"F0.wireOp",EDGE,"E3.MirrorC"),sQuery(id+"F0.wireOp",EDGE,"E26"),sQuery(id+"F0.wireOp",EDGE,"E27"),sQuery(id+"F0.wireOp",EDGE,"E75.MirrorCS"),sQuery(id+"F0.wireOp",EDGE,"E119.MirrorCS"),sQuery(id+"F0.wireOp",EDGE,"E166.trimOffspring"),sQuery(id+"F0.wireOp",EDGE,"E167.trimOffspring"),sQuery(id+"F0.wireOp",EDGE,"E191.trimOffspring"),sQuery(id+"F0.wireOp",EDGE,"E194"),sQuery(id+"F0.wireOp",EDGE,"E195"),sQuery(id+"F0.wireOp",EDGE,"E196")])]}),"instanceName":"12"});
            var Q10;
            Q10=makeQuery(id+"F2.opPattern","COPY",BODY,{"derivedFrom":makeQuery(id+"F1.opExtrude","SWEPT_BODY",BODY,{"disambiguationData":[OSD([sQuery(id+"F0.wireOp",EDGE,"E0"),sQuery(id+"F0.wireOp",EDGE,"E2"),sQuery(id+"F0.wireOp",EDGE,"E3.MirrorC"),sQuery(id+"F0.wireOp",EDGE,"E26"),sQuery(id+"F0.wireOp",EDGE,"E27"),sQuery(id+"F0.wireOp",EDGE,"E75.MirrorCS"),sQuery(id+"F0.wireOp",EDGE,"E119.MirrorCS"),sQuery(id+"F0.wireOp",EDGE,"E166.trimOffspring"),sQuery(id+"F0.wireOp",EDGE,"E167.trimOffspring"),sQuery(id+"F0.wireOp",EDGE,"E191.trimOffspring"),sQuery(id+"F0.wireOp",EDGE,"E194"),sQuery(id+"F0.wireOp",EDGE,"E195"),sQuery(id+"F0.wireOp",EDGE,"E196")])]}),"instanceName":"13"});
            var Q11;
            Q11=makeQuery(id+"F2.opPattern","COPY",BODY,{"derivedFrom":makeQuery(id+"F1.opExtrude","SWEPT_BODY",BODY,{"disambiguationData":[OSD([sQuery(id+"F0.wireOp",EDGE,"E0"),sQuery(id+"F0.wireOp",EDGE,"E2"),sQuery(id+"F0.wireOp",EDGE,"E3.MirrorC"),sQuery(id+"F0.wireOp",EDGE,"E26"),sQuery(id+"F0.wireOp",EDGE,"E27"),sQuery(id+"F0.wireOp",EDGE,"E75.MirrorCS"),sQuery(id+"F0.wireOp",EDGE,"E119.MirrorCS"),sQuery(id+"F0.wireOp",EDGE,"E166.trimOffspring"),sQuery(id+"F0.wireOp",EDGE,"E167.trimOffspring"),sQuery(id+"F0.wireOp",EDGE,"E191.trimOffspring"),sQuery(id+"F0.wireOp",EDGE,"E194"),sQuery(id+"F0.wireOp",EDGE,"E195"),sQuery(id+"F0.wireOp",EDGE,"E196")])]}),"instanceName":"14"});
            var Q12;
            Q12=makeQuery(id+"F2.opPattern","COPY",BODY,{"derivedFrom":makeQuery(id+"F1.opExtrude","SWEPT_BODY",BODY,{"disambiguationData":[OSD([sQuery(id+"F0.wireOp",EDGE,"E0"),sQuery(id+"F0.wireOp",EDGE,"E2"),sQuery(id+"F0.wireOp",EDGE,"E3.MirrorC"),sQuery(id+"F0.wireOp",EDGE,"E26"),sQuery(id+"F0.wireOp",EDGE,"E27"),sQuery(id+"F0.wireOp",EDGE,"E75.MirrorCS"),sQuery(id+"F0.wireOp",EDGE,"E119.MirrorCS"),sQuery(id+"F0.wireOp",EDGE,"E166.trimOffspring"),sQuery(id+"F0.wireOp",EDGE,"E167.trimOffspring"),sQuery(id+"F0.wireOp",EDGE,"E191.trimOffspring"),sQuery(id+"F0.wireOp",EDGE,"E194"),sQuery(id+"F0.wireOp",EDGE,"E195"),sQuery(id+"F0.wireOp",EDGE,"E196")])]}),"instanceName":"17"});
            var Q13;
            Q13=makeQuery(id+"F2.opPattern","COPY",BODY,{"derivedFrom":makeQuery(id+"F1.opExtrude","SWEPT_BODY",BODY,{"disambiguationData":[OSD([sQuery(id+"F0.wireOp",EDGE,"E0"),sQuery(id+"F0.wireOp",EDGE,"E2"),sQuery(id+"F0.wireOp",EDGE,"E3.MirrorC"),sQuery(id+"F0.wireOp",EDGE,"E26"),sQuery(id+"F0.wireOp",EDGE,"E27"),sQuery(id+"F0.wireOp",EDGE,"E75.MirrorCS"),sQuery(id+"F0.wireOp",EDGE,"E119.MirrorCS"),sQuery(id+"F0.wireOp",EDGE,"E166.trimOffspring"),sQuery(id+"F0.wireOp",EDGE,"E167.trimOffspring"),sQuery(id+"F0.wireOp",EDGE,"E191.trimOffspring"),sQuery(id+"F0.wireOp",EDGE,"E194"),sQuery(id+"F0.wireOp",EDGE,"E195"),sQuery(id+"F0.wireOp",EDGE,"E196")])]}),"instanceName":"18"});
            var Q14;
            Q14=makeQuery(id+"F2.opPattern","COPY",BODY,{"derivedFrom":makeQuery(id+"F1.opExtrude","SWEPT_BODY",BODY,{"disambiguationData":[OSD([sQuery(id+"F0.wireOp",EDGE,"E0"),sQuery(id+"F0.wireOp",EDGE,"E2"),sQuery(id+"F0.wireOp",EDGE,"E3.MirrorC"),sQuery(id+"F0.wireOp",EDGE,"E26"),sQuery(id+"F0.wireOp",EDGE,"E27"),sQuery(id+"F0.wireOp",EDGE,"E75.MirrorCS"),sQuery(id+"F0.wireOp",EDGE,"E119.MirrorCS"),sQuery(id+"F0.wireOp",EDGE,"E166.trimOffspring"),sQuery(id+"F0.wireOp",EDGE,"E167.trimOffspring"),sQuery(id+"F0.wireOp",EDGE,"E191.trimOffspring"),sQuery(id+"F0.wireOp",EDGE,"E194"),sQuery(id+"F0.wireOp",EDGE,"E195"),sQuery(id+"F0.wireOp",EDGE,"E196")])]}),"instanceName":"20"});
            var Q15;
            Q15=makeQuery(id+"F2.opPattern","COPY",BODY,{"derivedFrom":makeQuery(id+"F1.opExtrude","SWEPT_BODY",BODY,{"disambiguationData":[OSD([sQuery(id+"F0.wireOp",EDGE,"E0"),sQuery(id+"F0.wireOp",EDGE,"E2"),sQuery(id+"F0.wireOp",EDGE,"E3.MirrorC"),sQuery(id+"F0.wireOp",EDGE,"E26"),sQuery(id+"F0.wireOp",EDGE,"E27"),sQuery(id+"F0.wireOp",EDGE,"E75.MirrorCS"),sQuery(id+"F0.wireOp",EDGE,"E119.MirrorCS"),sQuery(id+"F0.wireOp",EDGE,"E166.trimOffspring"),sQuery(id+"F0.wireOp",EDGE,"E167.trimOffspring"),sQuery(id+"F0.wireOp",EDGE,"E191.trimOffspring"),sQuery(id+"F0.wireOp",EDGE,"E194"),sQuery(id+"F0.wireOp",EDGE,"E195"),sQuery(id+"F0.wireOp",EDGE,"E196")])]}),"instanceName":"21"});
            var Q16;
            Q16=makeQuery(id+"F2.opPattern","COPY",BODY,{"derivedFrom":makeQuery(id+"F1.opExtrude","SWEPT_BODY",BODY,{"disambiguationData":[OSD([sQuery(id+"F0.wireOp",EDGE,"E0"),sQuery(id+"F0.wireOp",EDGE,"E2"),sQuery(id+"F0.wireOp",EDGE,"E3.MirrorC"),sQuery(id+"F0.wireOp",EDGE,"E26"),sQuery(id+"F0.wireOp",EDGE,"E27"),sQuery(id+"F0.wireOp",EDGE,"E75.MirrorCS"),sQuery(id+"F0.wireOp",EDGE,"E119.MirrorCS"),sQuery(id+"F0.wireOp",EDGE,"E166.trimOffspring"),sQuery(id+"F0.wireOp",EDGE,"E167.trimOffspring"),sQuery(id+"F0.wireOp",EDGE,"E191.trimOffspring"),sQuery(id+"F0.wireOp",EDGE,"E194"),sQuery(id+"F0.wireOp",EDGE,"E195"),sQuery(id+"F0.wireOp",EDGE,"E196")])]}),"instanceName":"22"});
            var Q17;
            Q17=makeQuery(id+"F2.opPattern","COPY",BODY,{"derivedFrom":makeQuery(id+"F1.opExtrude","SWEPT_BODY",BODY,{"disambiguationData":[OSD([sQuery(id+"F0.wireOp",EDGE,"E0"),sQuery(id+"F0.wireOp",EDGE,"E2"),sQuery(id+"F0.wireOp",EDGE,"E3.MirrorC"),sQuery(id+"F0.wireOp",EDGE,"E26"),sQuery(id+"F0.wireOp",EDGE,"E27"),sQuery(id+"F0.wireOp",EDGE,"E75.MirrorCS"),sQuery(id+"F0.wireOp",EDGE,"E119.MirrorCS"),sQuery(id+"F0.wireOp",EDGE,"E166.trimOffspring"),sQuery(id+"F0.wireOp",EDGE,"E167.trimOffspring"),sQuery(id+"F0.wireOp",EDGE,"E191.trimOffspring"),sQuery(id+"F0.wireOp",EDGE,"E194"),sQuery(id+"F0.wireOp",EDGE,"E195"),sQuery(id+"F0.wireOp",EDGE,"E196")])]}),"instanceName":"23"});
            var Q18;
            Q18=makeQuery(id+"F2.opPattern","COPY",BODY,{"derivedFrom":makeQuery(id+"F1.opExtrude","SWEPT_BODY",BODY,{"disambiguationData":[OSD([sQuery(id+"F0.wireOp",EDGE,"E0"),sQuery(id+"F0.wireOp",EDGE,"E2"),sQuery(id+"F0.wireOp",EDGE,"E3.MirrorC"),sQuery(id+"F0.wireOp",EDGE,"E26"),sQuery(id+"F0.wireOp",EDGE,"E27"),sQuery(id+"F0.wireOp",EDGE,"E75.MirrorCS"),sQuery(id+"F0.wireOp",EDGE,"E119.MirrorCS"),sQuery(id+"F0.wireOp",EDGE,"E166.trimOffspring"),sQuery(id+"F0.wireOp",EDGE,"E167.trimOffspring"),sQuery(id+"F0.wireOp",EDGE,"E191.trimOffspring"),sQuery(id+"F0.wireOp",EDGE,"E194"),sQuery(id+"F0.wireOp",EDGE,"E195"),sQuery(id+"F0.wireOp",EDGE,"E196")])]}),"instanceName":"16"});
            var Q19;
            Q19=makeQuery(id+"F2.opPattern","COPY",BODY,{"derivedFrom":makeQuery(id+"F1.opExtrude","SWEPT_BODY",BODY,{"disambiguationData":[OSD([sQuery(id+"F0.wireOp",EDGE,"E0"),sQuery(id+"F0.wireOp",EDGE,"E2"),sQuery(id+"F0.wireOp",EDGE,"E3.MirrorC"),sQuery(id+"F0.wireOp",EDGE,"E26"),sQuery(id+"F0.wireOp",EDGE,"E27"),sQuery(id+"F0.wireOp",EDGE,"E75.MirrorCS"),sQuery(id+"F0.wireOp",EDGE,"E119.MirrorCS"),sQuery(id+"F0.wireOp",EDGE,"E166.trimOffspring"),sQuery(id+"F0.wireOp",EDGE,"E167.trimOffspring"),sQuery(id+"F0.wireOp",EDGE,"E191.trimOffspring"),sQuery(id+"F0.wireOp",EDGE,"E194"),sQuery(id+"F0.wireOp",EDGE,"E195"),sQuery(id+"F0.wireOp",EDGE,"E196")])]}),"instanceName":"15"});
            var Q20;
            Q20=makeQuery(id+"F2.opPattern","COPY",BODY,{"derivedFrom":makeQuery(id+"F1.opExtrude","SWEPT_BODY",BODY,{"disambiguationData":[OSD([sQuery(id+"F0.wireOp",EDGE,"E0"),sQuery(id+"F0.wireOp",EDGE,"E2"),sQuery(id+"F0.wireOp",EDGE,"E3.MirrorC"),sQuery(id+"F0.wireOp",EDGE,"E26"),sQuery(id+"F0.wireOp",EDGE,"E27"),sQuery(id+"F0.wireOp",EDGE,"E75.MirrorCS"),sQuery(id+"F0.wireOp",EDGE,"E119.MirrorCS"),sQuery(id+"F0.wireOp",EDGE,"E166.trimOffspring"),sQuery(id+"F0.wireOp",EDGE,"E167.trimOffspring"),sQuery(id+"F0.wireOp",EDGE,"E191.trimOffspring"),sQuery(id+"F0.wireOp",EDGE,"E194"),sQuery(id+"F0.wireOp",EDGE,"E195"),sQuery(id+"F0.wireOp",EDGE,"E196")])]}),"instanceName":"7"});
            var Q21;
            Q21=makeQuery(id+"F2.opPattern","COPY",BODY,{"derivedFrom":makeQuery(id+"F1.opExtrude","SWEPT_BODY",BODY,{"disambiguationData":[OSD([sQuery(id+"F0.wireOp",EDGE,"E0"),sQuery(id+"F0.wireOp",EDGE,"E2"),sQuery(id+"F0.wireOp",EDGE,"E3.MirrorC"),sQuery(id+"F0.wireOp",EDGE,"E26"),sQuery(id+"F0.wireOp",EDGE,"E27"),sQuery(id+"F0.wireOp",EDGE,"E75.MirrorCS"),sQuery(id+"F0.wireOp",EDGE,"E119.MirrorCS"),sQuery(id+"F0.wireOp",EDGE,"E166.trimOffspring"),sQuery(id+"F0.wireOp",EDGE,"E167.trimOffspring"),sQuery(id+"F0.wireOp",EDGE,"E191.trimOffspring"),sQuery(id+"F0.wireOp",EDGE,"E194"),sQuery(id+"F0.wireOp",EDGE,"E195"),sQuery(id+"F0.wireOp",EDGE,"E196")])]}),"instanceName":"5"});
            var Q22;
            Q22=makeQuery(id+"F2.opPattern","COPY",BODY,{"derivedFrom":makeQuery(id+"F1.opExtrude","SWEPT_BODY",BODY,{"disambiguationData":[OSD([sQuery(id+"F0.wireOp",EDGE,"E0"),sQuery(id+"F0.wireOp",EDGE,"E2"),sQuery(id+"F0.wireOp",EDGE,"E3.MirrorC"),sQuery(id+"F0.wireOp",EDGE,"E26"),sQuery(id+"F0.wireOp",EDGE,"E27"),sQuery(id+"F0.wireOp",EDGE,"E75.MirrorCS"),sQuery(id+"F0.wireOp",EDGE,"E119.MirrorCS"),sQuery(id+"F0.wireOp",EDGE,"E166.trimOffspring"),sQuery(id+"F0.wireOp",EDGE,"E167.trimOffspring"),sQuery(id+"F0.wireOp",EDGE,"E191.trimOffspring"),sQuery(id+"F0.wireOp",EDGE,"E194"),sQuery(id+"F0.wireOp",EDGE,"E195"),sQuery(id+"F0.wireOp",EDGE,"E196")])]}),"instanceName":"10"});
            var Q23;
            Q23=makeQuery(id+"F2.opPattern","COPY",BODY,{"derivedFrom":makeQuery(id+"F1.opExtrude","SWEPT_BODY",BODY,{"disambiguationData":[OSD([sQuery(id+"F0.wireOp",EDGE,"E0"),sQuery(id+"F0.wireOp",EDGE,"E2"),sQuery(id+"F0.wireOp",EDGE,"E3.MirrorC"),sQuery(id+"F0.wireOp",EDGE,"E26"),sQuery(id+"F0.wireOp",EDGE,"E27"),sQuery(id+"F0.wireOp",EDGE,"E75.MirrorCS"),sQuery(id+"F0.wireOp",EDGE,"E119.MirrorCS"),sQuery(id+"F0.wireOp",EDGE,"E166.trimOffspring"),sQuery(id+"F0.wireOp",EDGE,"E167.trimOffspring"),sQuery(id+"F0.wireOp",EDGE,"E191.trimOffspring"),sQuery(id+"F0.wireOp",EDGE,"E194"),sQuery(id+"F0.wireOp",EDGE,"E195"),sQuery(id+"F0.wireOp",EDGE,"E196")])]}),"instanceName":"19"});
            booleanBodies(context, id + "F3", {"operationType" : BooleanOperationType.UNION, "tools" : qUnion([Q0, Q1, Q2, Q3, Q4, Q5, Q6, Q7, Q8, Q9, Q10, Q11, Q12, Q13, Q14, Q15, Q16, Q17, Q18, Q19, Q20, Q21, Q22, Q23])});
        }
        {
            var Q0;
            {var subQ0=makeQuery(id+"F1.opExtrude","CAP_FACE",FACE,{"disambiguationData":[OSD([sQuery(id+"F0.wireOp",EDGE,"E0"),sQuery(id+"F0.wireOp",EDGE,"E2"),sQuery(id+"F0.wireOp",EDGE,"E3.MirrorC"),sQuery(id+"F0.wireOp",EDGE,"E26"),sQuery(id+"F0.wireOp",EDGE,"E27"),sQuery(id+"F0.wireOp",EDGE,"E75.MirrorCS"),sQuery(id+"F0.wireOp",EDGE,"E119.MirrorCS"),sQuery(id+"F0.wireOp",EDGE,"E166.trimOffspring"),sQuery(id+"F0.wireOp",EDGE,"E167.trimOffspring"),sQuery(id+"F0.wireOp",EDGE,"E191.trimOffspring"),sQuery(id+"F0.wireOp",EDGE,"E194"),sQuery(id+"F0.wireOp",EDGE,"E195"),sQuery(id+"F0.wireOp",EDGE,"E196")])],"isStart":false});Q0=makeQuery(id+"F3.opBoolean","MERGE",FACE,{"derivedFrom":[subQ0,makeQuery(id+"F2.opPattern","COPY",FACE,{"derivedFrom":subQ0,"instanceName":"1"}),makeQuery(id+"F2.opPattern","COPY",FACE,{"derivedFrom":subQ0,"instanceName":"2"}),makeQuery(id+"F2.opPattern","COPY",FACE,{"derivedFrom":subQ0,"instanceName":"3"}),makeQuery(id+"F2.opPattern","COPY",FACE,{"derivedFrom":subQ0,"instanceName":"4"}),makeQuery(id+"F2.opPattern","COPY",FACE,{"derivedFrom":subQ0,"instanceName":"5"}),makeQuery(id+"F2.opPattern","COPY",FACE,{"derivedFrom":subQ0,"instanceName":"6"}),makeQuery(id+"F2.opPattern","COPY",FACE,{"derivedFrom":subQ0,"instanceName":"7"}),makeQuery(id+"F2.opPattern","COPY",FACE,{"derivedFrom":subQ0,"instanceName":"8"}),makeQuery(id+"F2.opPattern","COPY",FACE,{"derivedFrom":subQ0,"instanceName":"9"}),makeQuery(id+"F2.opPattern","COPY",FACE,{"derivedFrom":subQ0,"instanceName":"10"}),makeQuery(id+"F2.opPattern","COPY",FACE,{"derivedFrom":subQ0,"instanceName":"11"}),makeQuery(id+"F2.opPattern","COPY",FACE,{"derivedFrom":subQ0,"instanceName":"12"}),makeQuery(id+"F2.opPattern","COPY",FACE,{"derivedFrom":subQ0,"instanceName":"13"}),makeQuery(id+"F2.opPattern","COPY",FACE,{"derivedFrom":subQ0,"instanceName":"14"}),makeQuery(id+"F2.opPattern","COPY",FACE,{"derivedFrom":subQ0,"instanceName":"15"}),makeQuery(id+"F2.opPattern","COPY",FACE,{"derivedFrom":subQ0,"instanceName":"16"}),makeQuery(id+"F2.opPattern","COPY",FACE,{"derivedFrom":subQ0,"instanceName":"17"}),makeQuery(id+"F2.opPattern","COPY",FACE,{"derivedFrom":subQ0,"instanceName":"18"}),makeQuery(id+"F2.opPattern","COPY",FACE,{"derivedFrom":subQ0,"instanceName":"19"}),makeQuery(id+"F2.opPattern","COPY",FACE,{"derivedFrom":subQ0,"instanceName":"20"}),makeQuery(id+"F2.opPattern","COPY",FACE,{"derivedFrom":subQ0,"instanceName":"21"}),makeQuery(id+"F2.opPattern","COPY",FACE,{"derivedFrom":subQ0,"instanceName":"22"}),makeQuery(id+"F2.opPattern","COPY",FACE,{"derivedFrom":subQ0,"instanceName":"23"})]});}
            var sketch = newSketch(context, id + "F4", { "sketchPlane" : qUnion([Q0])});
            skArc(sketch, "E197", {"start": v(16.25, 5) * mm, "mid": v(-17, 0) * mm, "end": v(16.25, -5) * mm});
            skLineSegment(sketch, "E198", {"start": v(21, 5) * mm, "end": v(16.25, 5) * mm});
            skLineSegment(sketch, "E199", {"start": v(16.25, -5) * mm, "end": v(21, -5) * mm});
            skLineSegment(sketch, "E200", {"start": v(21, 5) * mm, "end": v(21, -5) * mm});
            skSolve(sketch);
        }
        {
            var Q0;
            Q0 = qSketchRegion(id + "F4", true);
            extrude(context, id + "F5", {"entities" : qUnion([Q0]), "operationType" : NewBodyOperationType.REMOVE, "oppositeDirection" : true, "depth" : 50 * mm, "offsetDistance" : 25 * mm});
        }
        {
            var Q0;
            Q0 = qSketchRegion(id + "F4", true);
            extrude(context, id + "F6", {"entities" : qUnion([Q0]), "operationType" : NewBodyOperationType.REMOVE, "oppositeDirection" : true, "depth" : 50 * mm, "offsetDistance" : 25 * mm});
        }
    });
